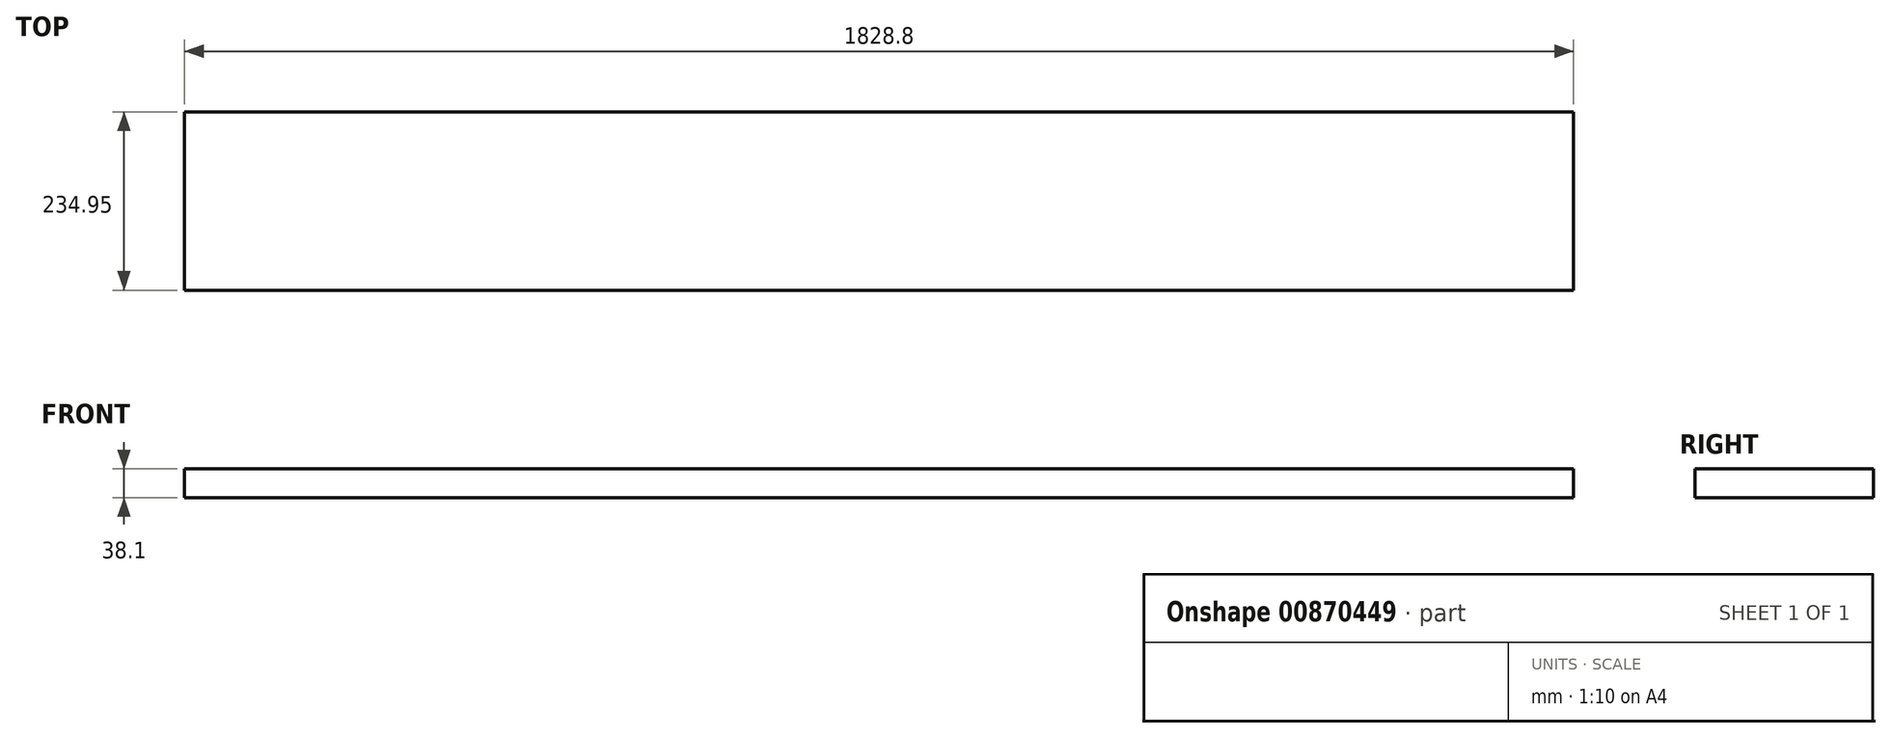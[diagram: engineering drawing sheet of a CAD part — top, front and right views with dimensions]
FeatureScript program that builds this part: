
annotation { "Feature Type Name" : "Feature", "Feature Type Description" : "" }
export const myFeature = defineFeature(function(context is Context, id is Id, definition is map)
    precondition{}
    {
        {
            var Q0;
            Q0=qCreatedBy(makeId("Right.planeOp"),FACE);
            var sketch = newSketch(context, id + "F0", { "sketchPlane" : qUnion([Q0])});
            skLineSegment(sketch, "E0.bottom", {"start": v(119.28, 19.05) * mm, "end": v(-115.67, 19.05) * mm});
            skLineSegment(sketch, "E0.top", {"start": v(119.28, -19.05) * mm, "end": v(-115.67, -19.05) * mm});
            skLineSegment(sketch, "E0.left", {"start": v(119.28, 19.05) * mm, "end": v(119.28, -19.05) * mm});
            skLineSegment(sketch, "E0.right", {"start": v(-115.67, 19.05) * mm, "end": v(-115.67, -19.05) * mm});
            skPoint(sketch, "E0.middle", {"position": v(1.8, 0) * mm});
            skSolve(sketch);
        }
        {
            var Q0;
            Q0=makeQuery(id+"F0.imprint","IMPRINT",FACE,{"disambiguationData":[TD([[makeQuery(id+"F0.imprint","IMPRINT",EDGE,{"derivedFrom":sQuery(id+"F0.wireOp",EDGE,"E0.bottom")}),1.0]])]});
            extrude(context, id + "F1", {"entities" : qUnion([Q0]), "depth" : 1828.8 * mm, "offsetDistance" : 25.4 * mm});
        }
    });
